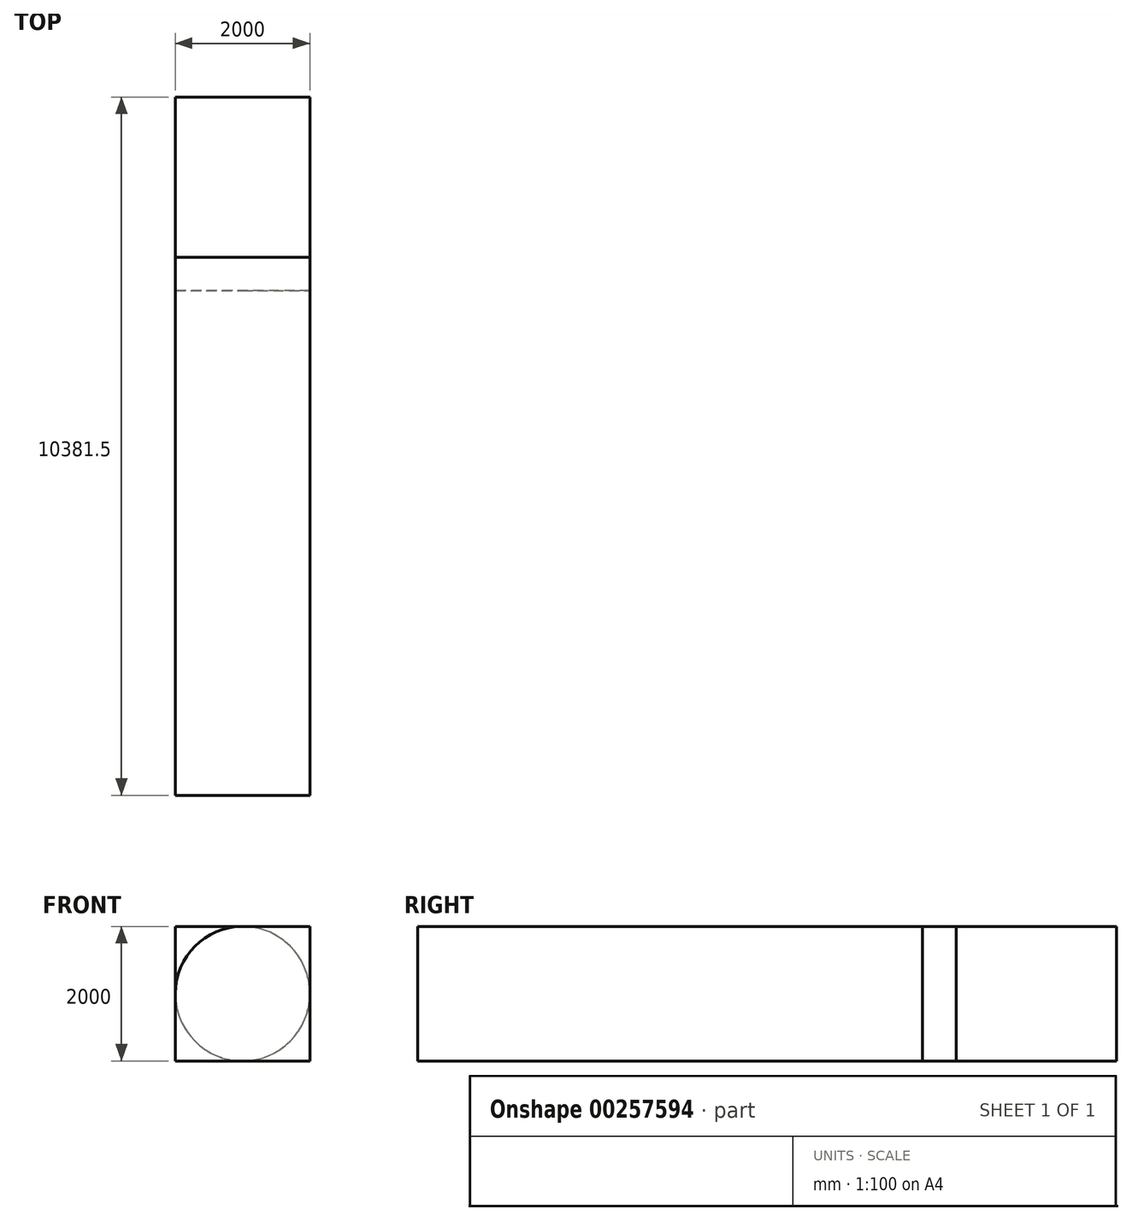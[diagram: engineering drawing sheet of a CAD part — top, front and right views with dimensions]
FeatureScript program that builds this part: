
annotation { "Feature Type Name" : "Feature", "Feature Type Description" : "" }
export const myFeature = defineFeature(function(context is Context, id is Id, definition is map)
    precondition{}
    {
        {
            var Q0;
            Q0=qCreatedBy(makeId("Right.planeOp"),FACE);
            var sketch = newSketch(context, id + "F0", { "sketchPlane" : qUnion([Q0])});
            skLineSegment(sketch, "E0.bottom", {"start": v(4000, 1000) * mm, "end": v(-4000, 1000) * mm});
            skLineSegment(sketch, "E0.top", {"start": v(4000, -1000) * mm, "end": v(-4000, -1000) * mm});
            skLineSegment(sketch, "E0.left", {"start": v(4000, 1000) * mm, "end": v(4000, -1000) * mm});
            skLineSegment(sketch, "E0.right", {"start": v(-4000, 1000) * mm, "end": v(-4000, -1000) * mm});
            skPoint(sketch, "E0.middle", {"position": v(0, 0) * mm});
            skSolve(sketch);
        }
        {
            var Q0;
            Q0=makeQuery(id+"F0.imprint","IMPRINT",FACE,{"disambiguationData":[TD([[makeQuery(id+"F0.imprint","IMPRINT",EDGE,{"derivedFrom":sQuery(id+"F0.wireOp",EDGE,"E0.bottom")}),1.0]])]});
            extrude(context, id + "F1", {"entities" : qUnion([Q0]), "endBound" : BoundingType.SYMMETRIC, "depth" : 2000 * mm});
        }
        {
            var Q0;
            Q0=makeQuery(id+"F1.opExtrude","SWEPT_FACE",FACE,{"disambiguationData":[OSD([sQuery(id+"F0.wireOp",EDGE,"E0.left")])]});
            var sketch = newSketch(context, id + "F2", { "sketchPlane" : qUnion([Q0])});
            skCircle(sketch, "E1", {"center": v(0, 0) * mm, "radius": 1000 * mm});
            skSolve(sketch);
        }
        {
            var Q0;
            {var subQ0=sQuery(id+"F2.wireOp",EDGE,"E1");var subQ1=sQuery(id+"F0.wireOp",EDGE,"E0.left");var subQ3=makeQuery(id+"F2.imprint","INTERSECT",VERTEX,{"derivedFrom":[makeQuery(id+"F1.opExtrude","CAP_EDGE",EDGE,{"disambiguationData":[OSD([subQ1])],"isStart":true}),subQ0]});Q0=makeQuery(id+"F2.imprint","IMPRINT",FACE,{"disambiguationData":[TD([[makeQuery(id+"F2.imprint","IMPRINT",EDGE,{"disambiguationData":[TD([[subQ3,-1.0]])],"derivedFrom":subQ0}),1.0]])]});}
            extrude(context, id + "F3", {"entities" : qUnion([Q0]), "depth" : 2381.46 * mm, "hasSecondDirection" : true, "secondDirectionOppositeDirection" : true, "secondDirectionDepth" : 500 * mm});
        }
    });
